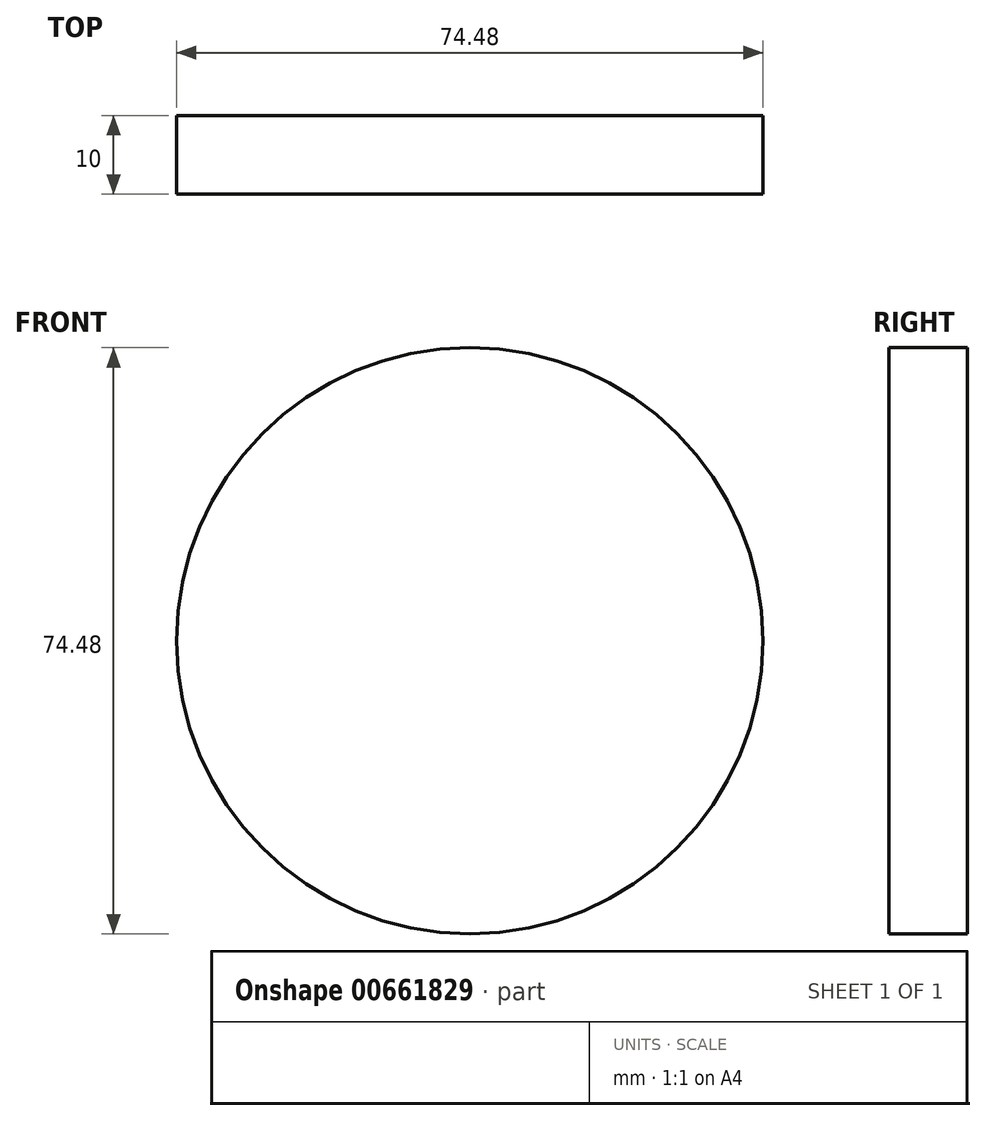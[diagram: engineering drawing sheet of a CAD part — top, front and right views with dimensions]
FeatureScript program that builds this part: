
annotation { "Feature Type Name" : "Feature", "Feature Type Description" : "" }
export const myFeature = defineFeature(function(context is Context, id is Id, definition is map)
    precondition{}
    {
        {
            var Q0;
            Q0=qCreatedBy(makeId("Front.planeOp"),FACE);
            var sketch = newSketch(context, id + "F0", { "sketchPlane" : qUnion([Q0])});
            skCircle(sketch, "E0", {"center": v(0, 0) * mm, "radius": 37.24 * mm});
            skSolve(sketch);
        }
        {
            var Q0;
            Q0=makeQuery(id+"F0.imprint","IMPRINT",FACE,{"disambiguationData":[TD([[makeQuery(id+"F0.imprint","IMPRINT",EDGE,{"derivedFrom":sQuery(id+"F0.wireOp",EDGE,"E0")}),1.0]])]});
            extrude(context, id + "F1", {"entities" : qUnion([Q0]), "oppositeDirection" : true, "depth" : 10 * mm, "offsetDistance" : 25 * mm});
        }
    });
